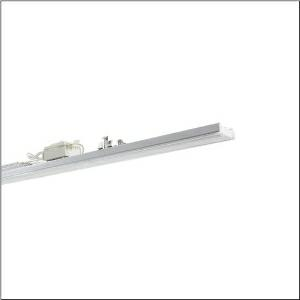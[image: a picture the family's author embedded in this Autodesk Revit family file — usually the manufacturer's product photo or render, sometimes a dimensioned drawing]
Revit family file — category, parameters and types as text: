
# Revit family: licross_r__11_recessed_mo_51tl10cn49xg_8b71
name_source: partatom
category: Lighting Fixtures
units: mm (PartAtom-declared; Revit-internal decimal feet)

## family parameters
Cut with Voids When Loaded = No
Host = Face
Light Source = No
Part Type = Normal
Room Calculation Point = No
Round Connector Dimension = Use Diameter
Shared = No

## types (1)
- --- (1 x LED, 9050 lm, 49.3 W, 4000K)
    Apparent Load = 49 VA
    CIE Flux Codes = 50 81 96 100 100
    Color Rendering = 80
    Color Temperature = 4000K
    Default Elevation = 1800 mm
    Description = Licross® 11 Recessed MO, luminaire insert, of sheet steel, coil coated, white, length: 1.500mm, width: 66mm, height: 67mm, LED rated luminous flux: 9.050lm, light colour: 840, control gear: ON/OFF Multilumen, CLOi, with plug, 3-pole, with phase selection, mains connection: 220..240V, AC, 50/60Hz, start of lifetime: 49W, end of service life: 55W, halogen-free wiring, primary optical cover: cover, of PMMA, light emission: direct distribution, primary light characteristic: symmetric, protection rating (complete): IP40, insulation class (complete): insulation class I (protective earthing), certification: CE, ENEC, VDE, UKCA, protection symbol: D if used in an environment without relevant dust loads with corresponding accessories, impact resistance: IK06, permissible ambient temperature for indoor applications: -35..+40°C, corresponds to IFS (International Featured Standards) requirements for safety and quality in the food industry, reducing of maximum allowable ambient temperature of 5°C with ceiling mounting, LABS conformity tested according to VDMA 24364:2018-05, packaging unit: 1 piece
    Height = 58 mm
    Lamp = 1 x LED
    Lamp Light Flux = 9050 lm
    Lamp Power = 49.3 W
    Lamp count = 1
    Length = 1500 mm
    Luminous efficacy = 184 lm/W
    Manufacturer = Siteco
    ModVariant = No
    Model = 51TL10CN49XG
    Mounting Place = Ceiling
    Mounting Type = Pendant
    Number of Poles = 1
    OnlyDefault = Yes
    Power Factor = 1
    Product Name = Licross® 11 Recessed MO
    Product group = luminaire insert
    ProductGroupID = 902
    Protection Class = Protection class I
    Protection Degree = IP 40
    RLX_Detail_Level = 1
    RLX_Emergency_Light_Flux = 0 lm
    RLX_Emergency_Type = 0
    RLX_Emergency_Type_DB = No
    RlxData = <blob elided: 22189 chars, md5=3cd15807>
    Socket = socket
    Standby Power = 0 W
    System Light Flux = 9050 lm
    System Power = 49 W
    Type Comments = factory setting: luminous flux: 100 % | (A | C | E) | 113 mA
    Type Image = l_1296930.jpg
    URL = http://relux.com
    VarID = @adj_085154
    Voltage = 0 V
    Weight = 0.00 kg
    Width = 66 mm

## geometry (parser evidence)
native form markers: Blend x4, Sweep x10
no freeform markers — native parametric forms only
